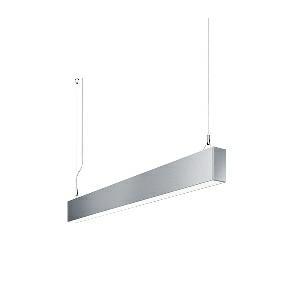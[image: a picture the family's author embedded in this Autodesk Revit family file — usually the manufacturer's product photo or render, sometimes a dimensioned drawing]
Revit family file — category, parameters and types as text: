
# Revit family: dotoo_line_-_dlp_1000_840_d_00805796_050f
name_source: partatom
category: Lighting Fixtures
units: mm (PartAtom-declared; Revit-internal decimal feet)

## family parameters
Cut with Voids When Loaded = No
Host = Face
Light Source = No
Part Type = Normal
Room Calculation Point = No
Round Connector Dimension = Use Diameter
Shared = No

## types (1)
- DOTOO.line - DLP 1000/840/D (1 x LED, 1000 lm, 4000K)
    Apparent Load = 10 VA
    Approval mark = CE
    CIE Flux Codes = 67 91 98 100 100
    Color Rendering = 80-89
    Color Temperature = 4000K
    Control Gear = Electronic ballast
    Default Elevation = 1800 mm
    Description = DLP 1000/840/D|Suspended luminaire|light source: LED|connected load: 220-240 V, 50/60 Hz|Power consumption: approx. 9,5 W|standby: approx. 0,20|luminous flux: 1000 lm|luminous efficacy: 105 lm/W|light distribution: Direct|direct ratio: approx. 100 %|colour temperature: Cold white, ca. 4000 K|color rendering index (CRI): >= 80|chromaticity tolerance:  3 SDCM|System of protection: IP 40|technology: Continuously dimmable|luminaire body|material: Sectional aluminium|colour: Silver|lamp cover: Acrylic (PMMA), Clear|mains lead: 2.00 m With free stranded wires|Fastening: Steel cable 0.3 - 0.7 m|glare control: Prism aperture|luminance(L65): <= 3000 cd/m|unified glare rating(4H 8H): <=  19|special features: DALI Load 1x, TouchDIM - dimming via standard switch, Flicker-free, Suitable as emergency lighting|
    Frequency = 50 Hz
    Height = 110 mm
    Lamp = 1 x LED
    Lamp Light Flux = 1000 lm
    Lamp count = 1
    Length = 854 mm
    Luminous efficacy = 105 lm/W
    Manufacturer = Waldmann
    ModVariant = No
    Model = 00805796
    Mounting Place = Ceiling
    Mounting Type = Pendant
    Number of Poles = 1
    OnlyDefault = Yes
    Power Factor = 1
    Product Name = DOTOO.line - DLP 1000/840/D
    Product group = Suspended luminaire
    ProductGroupID = 9
    Protection Class = Protection class I
    Protection Degree = IP 40
    RLX_Detail_Level = 1
    RLX_Emergency_Light_Flux = 0 lm
    RLX_Emergency_Type = 0
    RLX_Emergency_Type_DB = No
    RlxData = <blob elided: 19689 chars, md5=71f6a34f>
    Socket = socket
    Standby Power = 0 W
    System Light Flux = 1000 lm
    System Power = 10 W
    Type Comments = Product without accessories
    Type Image = 113288000-00692512.jpg
    URL = http://relux.com
    VarID = ---
    Voltage = 230 V
    Voltage Range = 220-240 V
    Weight = 0.00 kg
    Width = 60 mm  [stored 0.19685 ft]

note: [stored X ft] marks values corroborated as IEEE doubles in the binary element streams (Revit-internal decimal feet)

## geometry (parser evidence)
native form markers: Blend x4, Sweep x13
no freeform markers — native parametric forms only
